# Revit family: DVN
name_source: partatom
category: Wyposażenie mechaniczne
revit_build: Autodesk Revit 2017 (Build: 20160225_1515(x64)
units: mm (PartAtom-declared; Revit-internal decimal feet)

## family parameters
Oparty na płaszczyźnie roboczej = Nie
Punkt obliczania pomieszczeń = Nie
Tnij formami wycięć po wczytaniu = Nie
Typ części = Normalny
Współdzielony = Nie
Wymiar okrągłego złącza = Użyj średnicy
Zawsze pionowo = Tak

## types (27) — shared parameters
Air_flow = 0.0 m³/h
Date = 11.2018
Frequency = 50 Hz
Iniet_Collar = Tak
Pressure = 0.0 Pa
Producent = Rosenberg
Shutter_Automatic = Tak
Socket_Sound_Attenuator = Tak
URL = https://www.rosenberg.pl
Version = 1

## per-type parameters (varying)
| type | A | Current | Da | Di | H | Height | Height_1 | Height_2 | L | P | Power | Protection_class | Voltage | W1 | W2 | W3 | Weight[kg] | Width | Width_bottom | max.Ambient_temperature | t1 |
| 310L-4 E | 395 mm  [stored 1.29593 ft] | 1 A | 306 mm  [stored 1.00394 ft] | 256 mm  [stored 0.839895 ft] | 700 mm  [stored 2.29659 ft] | 350 mm  [stored 1.14829 ft] | 450 mm  [stored 1.47638 ft] | 90 mm | 156 mm  [stored 0.511811 ft] | 657 mm | 0 kW | IP54 | 230 V | 700 mm  [stored 2.29659 ft] | 156 mm  [stored 0.511811 ft] | 156 mm  [stored 0.511811 ft] | 19 | 560 mm  [stored 1.83727 ft] | 435 mm  [stored 1.42717 ft] | 120 °C | 2 mm  [stored 0.00656168 ft] |
| 355-4 E | 555 mm  [stored 1.82087 ft] | 2 A | 464 mm  [stored 1.52231 ft] | 402 mm  [stored 1.3189 ft] | 900 mm | 390 mm  [stored 1.27953 ft] | 550 mm | 150 mm  [stored 0.492126 ft] | 220 mm  [stored 0.721785 ft] | 817 mm  [stored 2.68045 ft] | 0 kW | IP54 | 230 V | 900 mm | 220 mm  [stored 0.721785 ft] | 220 mm  [stored 0.721785 ft] | 35 | 720 mm  [stored 2.3622 ft] | 595 mm  [stored 1.9521 ft] | 120 °C | 2 mm  [stored 0.00656168 ft] |
| 400-4 E | 555 mm  [stored 1.82087 ft] | 2 A | 464 mm  [stored 1.52231 ft] | 402 mm  [stored 1.3189 ft] | 900 mm | 390 mm  [stored 1.27953 ft] | 550 mm | 150 mm  [stored 0.492126 ft] | 220 mm  [stored 0.721785 ft] | 817 mm  [stored 2.68045 ft] | 1 kW | IP54 | 230 V | 900 mm | 220 mm  [stored 0.721785 ft] | 220 mm  [stored 0.721785 ft] | 40 | 720 mm  [stored 2.3622 ft] | 595 mm  [stored 1.9521 ft] | 120 °C | 2 mm  [stored 0.00656168 ft] |
| 450-4 E | 625 mm  [stored 2.05052 ft] | 4 A | 464 mm  [stored 1.52231 ft] | 402 mm  [stored 1.3189 ft] | 900 mm | 450 mm  [stored 1.47638 ft] | 550 mm | 90 mm | 220 mm  [stored 0.721785 ft] | 877 mm  [stored 2.8773 ft] | 1 kW | IP54 | 230 V | 900 mm | 220 mm  [stored 0.721785 ft] | 220 mm  [stored 0.721785 ft] | 49.5 | 900 mm | 665 mm  [stored 2.18176 ft] | 120 °C | 2 mm  [stored 0.00656168 ft] |
| 500-4 D | 625 mm  [stored 2.05052 ft] | 3 A | 464 mm  [stored 1.52231 ft] | 402 mm  [stored 1.3189 ft] | 900 mm | 450 mm  [stored 1.47638 ft] | 550 mm | 90 mm | 220 mm  [stored 0.721785 ft] | 877 mm  [stored 2.8773 ft] | 2 kW | IP55 | 400 V | 900 mm | 220 mm  [stored 0.721785 ft] | 220 mm  [stored 0.721785 ft] | 57.5 | 900 mm | 665 mm  [stored 2.18176 ft] | 120 °C | 2 mm  [stored 0.00656168 ft] |
| 560-4 D | 895 mm  [stored 2.93635 ft] | 5 A | 639 mm  [stored 2.09646 ft] | 569 mm  [stored 1.8668 ft] | 1070 mm | 520 mm  [stored 1.70604 ft] | 850 mm  [stored 2.78871 ft] | 320 mm  [stored 1.04987 ft] | 255 mm  [stored 0.836614 ft] | 1200 mm | 3 kW | IP55 | 400 V | 1070 mm | 255 mm  [stored 0.836614 ft] | 255 mm  [stored 0.836614 ft] | 105 | 1150 mm | 939 mm | 120 °C | 2 mm  [stored 0.00656168 ft] |
| 630-4 D | 895 mm  [stored 2.93635 ft] | 11 A | 639 mm  [stored 2.09646 ft] | 569 mm  [stored 1.8668 ft] | 1070 mm | 520 mm  [stored 1.70604 ft] | 850 mm  [stored 2.78871 ft] | 320 mm  [stored 1.04987 ft] | 255 mm  [stored 0.836614 ft] | 1200 mm | 6 kW | IP55 | 400 V | 1070 mm | 255 mm  [stored 0.836614 ft] | 255 mm  [stored 0.836614 ft] | 102 | 1150 mm | 939 mm | 120 °C | 2 mm  [stored 0.00656168 ft] |
| 710-6 D | 985 mm | 10 A | 708 mm  [stored 2.32283 ft] | 635 mm | 1160 mm | 660 mm | 950 mm | 280 mm  [stored 0.918635 ft] | 250 mm  [stored 0.82021 ft] | 1300 mm | 3 kW | IP55 | 400 V | 1160 mm | 250 mm  [stored 0.82021 ft] | 250 mm  [stored 0.82021 ft] | 149 | 1350 mm | 1035 mm | 120 °C | 4 mm  [stored 0.0131234 ft] |
| 310L-4 D | 395 mm  [stored 1.29593 ft] | 1 A | 306 mm  [stored 1.00394 ft] | 256 mm  [stored 0.839895 ft] | 700 mm  [stored 2.29659 ft] | 350 mm  [stored 1.14829 ft] | 450 mm  [stored 1.47638 ft] | 90 mm | 156 mm  [stored 0.511811 ft] | 657 mm | 0 kW | IP54 | 400 V | 700 mm  [stored 2.29659 ft] | 156 mm  [stored 0.511811 ft] | 156 mm  [stored 0.511811 ft] | 19 | 560 mm  [stored 1.83727 ft] | 435 mm  [stored 1.42717 ft] | 120 °C | 2 mm  [stored 0.00656168 ft] |
| 355-4 D | 555 mm  [stored 1.82087 ft] | 1 A | 464 mm  [stored 1.52231 ft] | 402 mm  [stored 1.3189 ft] | 900 mm | 390 mm  [stored 1.27953 ft] | 550 mm | 150 mm  [stored 0.492126 ft] | 220 mm  [stored 0.721785 ft] | 817 mm  [stored 2.68045 ft] | 0 kW | IP55 | 400 V | 900 mm | 220 mm  [stored 0.721785 ft] | 220 mm  [stored 0.721785 ft] | 35 | 720 mm  [stored 2.3622 ft] | 595 mm  [stored 1.9521 ft] | 120 °C | 2 mm  [stored 0.00656168 ft] |
| 400-4 D | 555 mm  [stored 1.82087 ft] | 1 A | 464 mm  [stored 1.52231 ft] | 402 mm  [stored 1.3189 ft] | 900 mm | 390 mm  [stored 1.27953 ft] | 550 mm | 150 mm  [stored 0.492126 ft] | 220 mm  [stored 0.721785 ft] | 817 mm  [stored 2.68045 ft] | 1 kW | IP54 | 400 V | 900 mm | 220 mm  [stored 0.721785 ft] | 220 mm  [stored 0.721785 ft] | 40 | 720 mm  [stored 2.3622 ft] | 595 mm  [stored 1.9521 ft] | 120 °C | 2 mm  [stored 0.00656168 ft] |
| 450-4 D | 625 mm  [stored 2.05052 ft] | 2 A | 464 mm  [stored 1.52231 ft] | 402 mm  [stored 1.3189 ft] | 900 mm | 450 mm  [stored 1.47638 ft] | 550 mm | 90 mm | 220 mm  [stored 0.721785 ft] | 877 mm  [stored 2.8773 ft] | 1 kW | IP55 | 400 V | 900 mm | 220 mm  [stored 0.721785 ft] | 220 mm  [stored 0.721785 ft] | 49.5 | 900 mm | 665 mm  [stored 2.18176 ft] | 120 °C | 2 mm  [stored 0.00656168 ft] |
| 800-6 D | 985 mm | 12 A | 708 mm  [stored 2.32283 ft] | 635 mm | 1160 mm | 845 mm  [stored 2.77231 ft] | 1150 mm | 295 mm | 250 mm  [stored 0.82021 ft] | 1300 mm | 5 kW | IP55 | 400 V | 1160 mm | 250 mm  [stored 0.82021 ft] | 250 mm  [stored 0.82021 ft] | 180 | 1700 mm | 1250 mm | 100 °C | 4 mm  [stored 0.0131234 ft] |
| 900-6 D | 985 mm | 17 A | 708 mm  [stored 2.32283 ft] | 635 mm | 1160 mm | 845 mm  [stored 2.77231 ft] | 1150 mm | 295 mm | 250 mm  [stored 0.82021 ft] | 1300 mm | 8 kW | IP54 | 400 V | 1160 mm | 250 mm  [stored 0.82021 ft] | 250 mm  [stored 0.82021 ft] | 308 | 1700 mm | 1250 mm | 100 °C | 4 mm  [stored 0.0131234 ft] |
| 900-8 D | 985 mm | 8 A | 708 mm  [stored 2.32283 ft] | 635 mm | 1160 mm | 845 mm  [stored 2.77231 ft] | 1150 mm | 295 mm | 250 mm  [stored 0.82021 ft] | 1300 mm | 3 kW | IP54 | 400 V | 1160 mm | 250 mm  [stored 0.82021 ft] | 250 mm  [stored 0.82021 ft] | 270 | 1700 mm | 1250 mm | 120 °C | 4 mm  [stored 0.0131234 ft] |
| 355-4D Exde | 555 mm  [stored 1.82087 ft] | 1 A | 464 mm  [stored 1.52231 ft] | 402 mm  [stored 1.3189 ft] | 900 mm | 390 mm  [stored 1.27953 ft] | 550 mm | 150 mm  [stored 0.492126 ft] | 220 mm  [stored 0.721785 ft] | 817 mm  [stored 2.68045 ft] | 1 kW | IP55 | 400 V | 900 mm | 220 mm  [stored 0.721785 ft] | 220 mm  [stored 0.721785 ft] | 35 | 720 mm  [stored 2.3622 ft] | 595 mm  [stored 1.9521 ft] | 40 °C | 2 mm  [stored 0.00656168 ft] |
| 355-4D Exe | 555 mm  [stored 1.82087 ft] | 2 A | 464 mm  [stored 1.52231 ft] | 402 mm  [stored 1.3189 ft] | 900 mm | 390 mm  [stored 1.27953 ft] | 550 mm | 150 mm  [stored 0.492126 ft] | 220 mm  [stored 0.721785 ft] | 817 mm  [stored 2.68045 ft] | 1 kW | IP55 | 400 V | 900 mm | 220 mm  [stored 0.721785 ft] | 220 mm  [stored 0.721785 ft] | 35 | 720 mm  [stored 2.3622 ft] | 595 mm  [stored 1.9521 ft] | 40 °C | 2 mm  [stored 0.00656168 ft] |
| 400-4D Exde | 555 mm  [stored 1.82087 ft] | 1 A | 464 mm  [stored 1.52231 ft] | 402 mm  [stored 1.3189 ft] | 900 mm | 390 mm  [stored 1.27953 ft] | 550 mm | 150 mm  [stored 0.492126 ft] | 220 mm  [stored 0.721785 ft] | 817 mm  [stored 2.68045 ft] | 1 kW | IP55 | 400 V | 900 mm | 220 mm  [stored 0.721785 ft] | 220 mm  [stored 0.721785 ft] | 40 | 720 mm  [stored 2.3622 ft] | 595 mm  [stored 1.9521 ft] | 40 °C | 2 mm  [stored 0.00656168 ft] |
| 400-4D Exe | 555 mm  [stored 1.82087 ft] | 1 A | 464 mm  [stored 1.52231 ft] | 402 mm  [stored 1.3189 ft] | 900 mm | 390 mm  [stored 1.27953 ft] | 550 mm | 150 mm  [stored 0.492126 ft] | 220 mm  [stored 0.721785 ft] | 817 mm  [stored 2.68045 ft] | 1 kW | IP55 | 400 V | 900 mm | 220 mm  [stored 0.721785 ft] | 220 mm  [stored 0.721785 ft] | 40 | 720 mm  [stored 2.3622 ft] | 595 mm  [stored 1.9521 ft] | 40 °C | 2 mm  [stored 0.00656168 ft] |
| 450-4D Exe | 625 mm  [stored 2.05052 ft] | 2 A | 464 mm  [stored 1.52231 ft] | 402 mm  [stored 1.3189 ft] | 900 mm | 450 mm  [stored 1.47638 ft] | 550 mm | 90 mm | 220 mm  [stored 0.721785 ft] | 877 mm  [stored 2.8773 ft] | 1 kW | IP55 | 400 V | 900 mm | 220 mm  [stored 0.721785 ft] | 220 mm  [stored 0.721785 ft] | 49.5 | 900 mm | 665 mm  [stored 2.18176 ft] | 4 °C | 2 mm  [stored 0.00656168 ft] |
| 450-4D Exde | 625 mm  [stored 2.05052 ft] | 2 A | 464 mm  [stored 1.52231 ft] | 402 mm  [stored 1.3189 ft] | 900 mm | 450 mm  [stored 1.47638 ft] | 550 mm | 90 mm | 220 mm  [stored 0.721785 ft] | 877 mm  [stored 2.8773 ft] | 1 kW | IP55 | 400 V | 900 mm | 220 mm  [stored 0.721785 ft] | 220 mm  [stored 0.721785 ft] | 49.5 | 900 mm | 665 mm  [stored 2.18176 ft] | 40 °C | 2 mm  [stored 0.00656168 ft] |
| 500-4D Exde | 625 mm  [stored 2.05052 ft] | 5 A | 464 mm  [stored 1.52231 ft] | 402 mm  [stored 1.3189 ft] | 900 mm | 450 mm  [stored 1.47638 ft] | 550 mm | 90 mm | 220 mm  [stored 0.721785 ft] | 877 mm  [stored 2.8773 ft] | 2 kW | IP55 | 400 V | 900 mm | 220 mm  [stored 0.721785 ft] | 220 mm  [stored 0.721785 ft] | 57.5 | 900 mm | 665 mm  [stored 2.18176 ft] | 40 °C | 2 mm  [stored 0.00656168 ft] |
| 500-4D Exe | 625 mm  [stored 2.05052 ft] | 5 A | 464 mm  [stored 1.52231 ft] | 402 mm  [stored 1.3189 ft] | 900 mm | 450 mm  [stored 1.47638 ft] | 550 mm | 90 mm | 220 mm  [stored 0.721785 ft] | 877 mm  [stored 2.8773 ft] | 2 kW | IP55 | 400 V | 900 mm | 220 mm  [stored 0.721785 ft] | 220 mm  [stored 0.721785 ft] | 57.5 | 900 mm | 665 mm  [stored 2.18176 ft] | 40 °C | 2 mm  [stored 0.00656168 ft] |
| 560-4D Exde | 895 mm  [stored 2.93635 ft] | 7 A | 639 mm  [stored 2.09646 ft] | 569 mm  [stored 1.8668 ft] | 1070 mm | 520 mm  [stored 1.70604 ft] | 850 mm  [stored 2.78871 ft] | 320 mm  [stored 1.04987 ft] | 255 mm  [stored 0.836614 ft] | 1200 mm | 3 kW | IP55 | 400 V | 1070 mm | 255 mm  [stored 0.836614 ft] | 255 mm  [stored 0.836614 ft] | 105 | 1150 mm | 939 mm | 40 °C | 2 mm  [stored 0.00656168 ft] |
| 560-4D Exe | 895 mm  [stored 2.93635 ft] | 8 A | 639 mm  [stored 2.09646 ft] | 569 mm  [stored 1.8668 ft] | 1070 mm | 520 mm  [stored 1.70604 ft] | 850 mm  [stored 2.78871 ft] | 320 mm  [stored 1.04987 ft] | 255 mm  [stored 0.836614 ft] | 1200 mm | 4 kW | IP55 | 400 V | 1070 mm | 255 mm  [stored 0.836614 ft] | 255 mm  [stored 0.836614 ft] | 105 | 1150 mm | 939 mm | 40 °C | 2 mm  [stored 0.00656168 ft] |
| 630-4D Exde | 895 mm  [stored 2.93635 ft] | 11 A | 639 mm  [stored 2.09646 ft] | 569 mm  [stored 1.8668 ft] | 1070 mm | 520 mm  [stored 1.70604 ft] | 850 mm  [stored 2.78871 ft] | 320 mm  [stored 1.04987 ft] | 255 mm  [stored 0.836614 ft] | 1200 mm | 6 kW | IP55 | 400 V | 1070 mm | 255 mm  [stored 0.836614 ft] | 255 mm  [stored 0.836614 ft] | 102 | 1150 mm | 939 mm | 40 °C | 2 mm  [stored 0.00656168 ft] |
| 630-4D Exe | 895 mm  [stored 2.93635 ft] | 10 A | 639 mm  [stored 2.09646 ft] | 569 mm  [stored 1.8668 ft] | 1070 mm | 520 mm  [stored 1.70604 ft] | 850 mm  [stored 2.78871 ft] | 320 mm  [stored 1.04987 ft] | 255 mm  [stored 0.836614 ft] | 1200 mm | 5 kW | IP55 | 400 V | 1070 mm | 255 mm  [stored 0.836614 ft] | 255 mm  [stored 0.836614 ft] | 102 | 1150 mm | 939 mm | 40 °C | 2 mm  [stored 0.00656168 ft] |

note: column(s) folded — value = type name in every type: Model

note: [stored X ft] marks values corroborated as IEEE doubles in the binary element streams (Revit-internal decimal feet)
